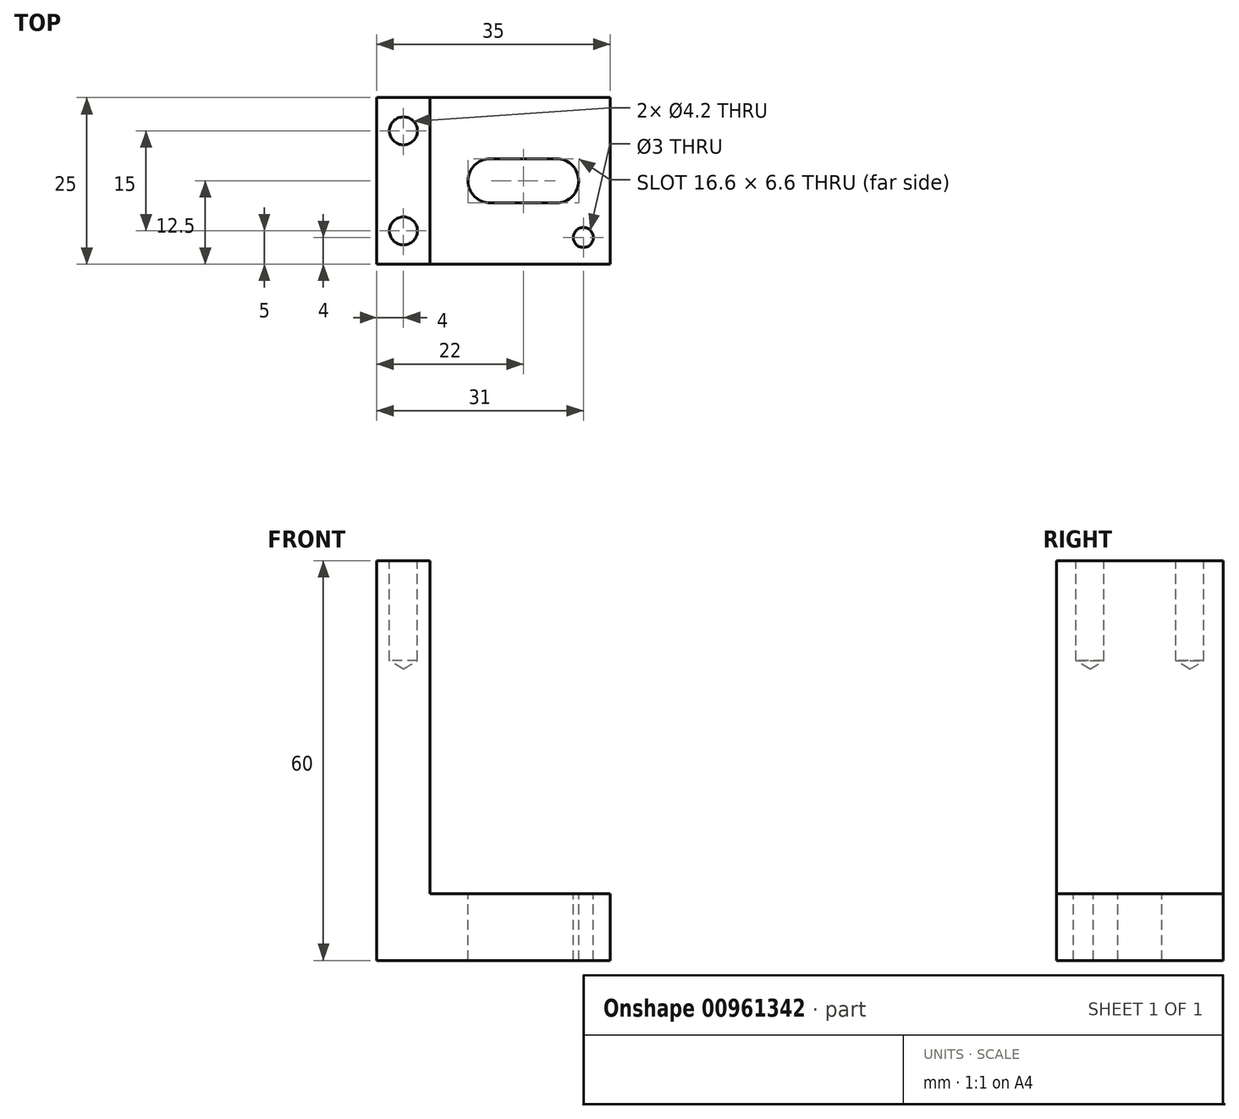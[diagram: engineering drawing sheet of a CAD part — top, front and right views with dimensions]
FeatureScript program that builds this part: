
annotation { "Feature Type Name" : "Feature", "Feature Type Description" : "" }
export const myFeature = defineFeature(function(context is Context, id is Id, definition is map)
    precondition{}
    {
        {
            var Q0;
            Q0=qCreatedBy(makeId("Front.planeOp"),FACE);
            var sketch = newSketch(context, id + "F0", { "sketchPlane" : qUnion([Q0])});
            skLineSegment(sketch, "E0", {"start": v(0, 0) * mm, "end": v(0, 60) * mm});
            skLineSegment(sketch, "E1", {"start": v(0, 60) * mm, "end": v(8, 60) * mm});
            skLineSegment(sketch, "E2", {"start": v(0, 0) * mm, "end": v(35, 0) * mm});
            skLineSegment(sketch, "E3", {"start": v(35, 10) * mm, "end": v(35, 0) * mm});
            skLineSegment(sketch, "E4", {"start": v(35, 10) * mm, "end": v(8, 10) * mm});
            skLineSegment(sketch, "E5", {"start": v(8, 10) * mm, "end": v(8, 60) * mm});
            skSolve(sketch);
        }
        {
            var Q0;
            Q0=makeQuery(id+"F0.imprint","IMPRINT",FACE,{"disambiguationData":[TD([[makeQuery(id+"F0.imprint","IMPRINT",EDGE,{"derivedFrom":sQuery(id+"F0.wireOp",EDGE,"E0")}),-1.0]])]});
            extrude(context, id + "F1", {"entities" : qUnion([Q0]), "depth" : 25 * mm, "offsetDistance" : 25 * mm});
        }
        {
            var Q0;
            Q0=makeQuery(id+"F1.opExtrude","SWEPT_FACE",FACE,{"disambiguationData":[OSD([sQuery(id+"F0.wireOp",EDGE,"E1")])]});
            var sketch = newSketch(context, id + "F2", { "sketchPlane" : qUnion([Q0])});
            skPoint(sketch, "E6", {"position": v(4, -5) * mm});
            skPoint(sketch, "E6.positionSnap0", {"position": v(4, 0) * mm});
            skPoint(sketch, "E7", {"position": v(4, -20) * mm});
            skSolve(sketch);
        }
        {
            var Q0;
            Q0=sQuery(id+"F2.wireOp",VERTEX,"E6");
            var Q1;
            Q1=sQuery(id+"F2.wireOp",VERTEX,"E7");
            var Q2;
            Q2=makeQuery(id+"F1.opExtrude","SWEPT_BODY",BODY,{"disambiguationData":[OSD([sQuery(id+"F0.wireOp",EDGE,"E0"),sQuery(id+"F0.wireOp",EDGE,"E1"),sQuery(id+"F0.wireOp",EDGE,"E2"),sQuery(id+"F0.wireOp",EDGE,"E3"),sQuery(id+"F0.wireOp",EDGE,"E4"),sQuery(id+"F0.wireOp",EDGE,"E5")])]});
            hole(context, id + "F3", {"style" : HoleStyle.SIMPLE, "endStyle" : HoleEndStyle.BLIND, "standardTappedOrClearance" : lookupTablePath({ "standard" : "ISO", "engagement" : "75%", "pitch" : "0.8 mm", "size" : "M5", "type" : "Tapped" }), "standardBlindInLast" : lookupTablePath({ "standard" : "ISO", "fit" : "Normal", "engagement" : "75%", "pitch" : "0.8 mm", "size" : "M5", "type" : "Clearance & tapped" }), "holeDiameter" : 4.2 * mm, "majorDiameter" : 5 * mm, "showTappedDepth" : true, "holeDepth" : 15 * mm, "isTappedThrough" : true, "tappedDepth" : 12.6 * mm, "tapClearance" : 3, "startFromSketch" : true, "locations" : qUnion([Q0, Q1]), "scope" : qUnion([Q2])});
        }
        {
            var Q0;
            Q0=makeQuery(id+"F1.opExtrude","SWEPT_FACE",FACE,{"disambiguationData":[OSD([sQuery(id+"F0.wireOp",EDGE,"E4")])]});
            var sketch = newSketch(context, id + "F4", { "sketchPlane" : qUnion([Q0])});
            skPoint(sketch, "E8", {"position": v(27, -12.5) * mm});
            skPoint(sketch, "E8.positionSnap0", {"position": v(8, -12.5) * mm});
            skPoint(sketch, "E9", {"position": v(17, -12.5) * mm});
            skPoint(sketch, "E10", {"position": v(35, -25) * mm});
            skCircle(sketch, "E11", {"center": v(27, -12.5) * mm, "radius": 3.3 * mm});
            skCircle(sketch, "E12", {"center": v(17, -12.5) * mm, "radius": 3.3 * mm});
            skLineSegment(sketch, "E13", {"start": v(27, -9.2) * mm, "end": v(27, -15.8) * mm});
            skLineSegment(sketch, "E14", {"start": v(27, -15.8) * mm, "end": v(17, -15.8) * mm});
            skLineSegment(sketch, "E15", {"start": v(17, -9.2) * mm, "end": v(27, -9.2) * mm});
            skPoint(sketch, "E16", {"position": v(31, -21) * mm});
            skSolve(sketch);
        }
        {
            var Q0;
            Q0 = qSketchRegion(id + "F4", true);
            extrude(context, id + "F5", {"entities" : qUnion([Q0]), "operationType" : NewBodyOperationType.REMOVE, "oppositeDirection" : true, "depth" : 25 * mm, "offsetDistance" : 25 * mm});
        }
        {
            var Q0;
            Q0=sQuery(id+"F4.wireOp",VERTEX,"E16");
            var Q1;
            Q1=makeQuery(id+"F1.opExtrude","SWEPT_BODY",BODY,{"disambiguationData":[OSD([sQuery(id+"F0.wireOp",EDGE,"E0"),sQuery(id+"F0.wireOp",EDGE,"E1"),sQuery(id+"F0.wireOp",EDGE,"E2"),sQuery(id+"F0.wireOp",EDGE,"E3"),sQuery(id+"F0.wireOp",EDGE,"E4"),sQuery(id+"F0.wireOp",EDGE,"E5")])]});
            hole(context, id + "F6", {"style" : HoleStyle.SIMPLE, "endStyle" : HoleEndStyle.BLIND, "standardTappedOrClearance" : lookupTablePath({ "standard" : "ISO", "size" : "3", "type" : "Drilled" }), "standardBlindInLast" : lookupTablePath({ "standard" : "ISO", "size" : "3", "type" : "Drilled" }), "holeDiameter" : 3 * mm, "majorDiameter" : 5 * mm, "holeDepth" : 15 * mm, "isTappedThrough" : true, "tappedDepth" : 12.6 * mm, "tapClearance" : 3, "startFromSketch" : true, "locations" : qUnion([Q0]), "scope" : qUnion([Q1])});
        }
    });
